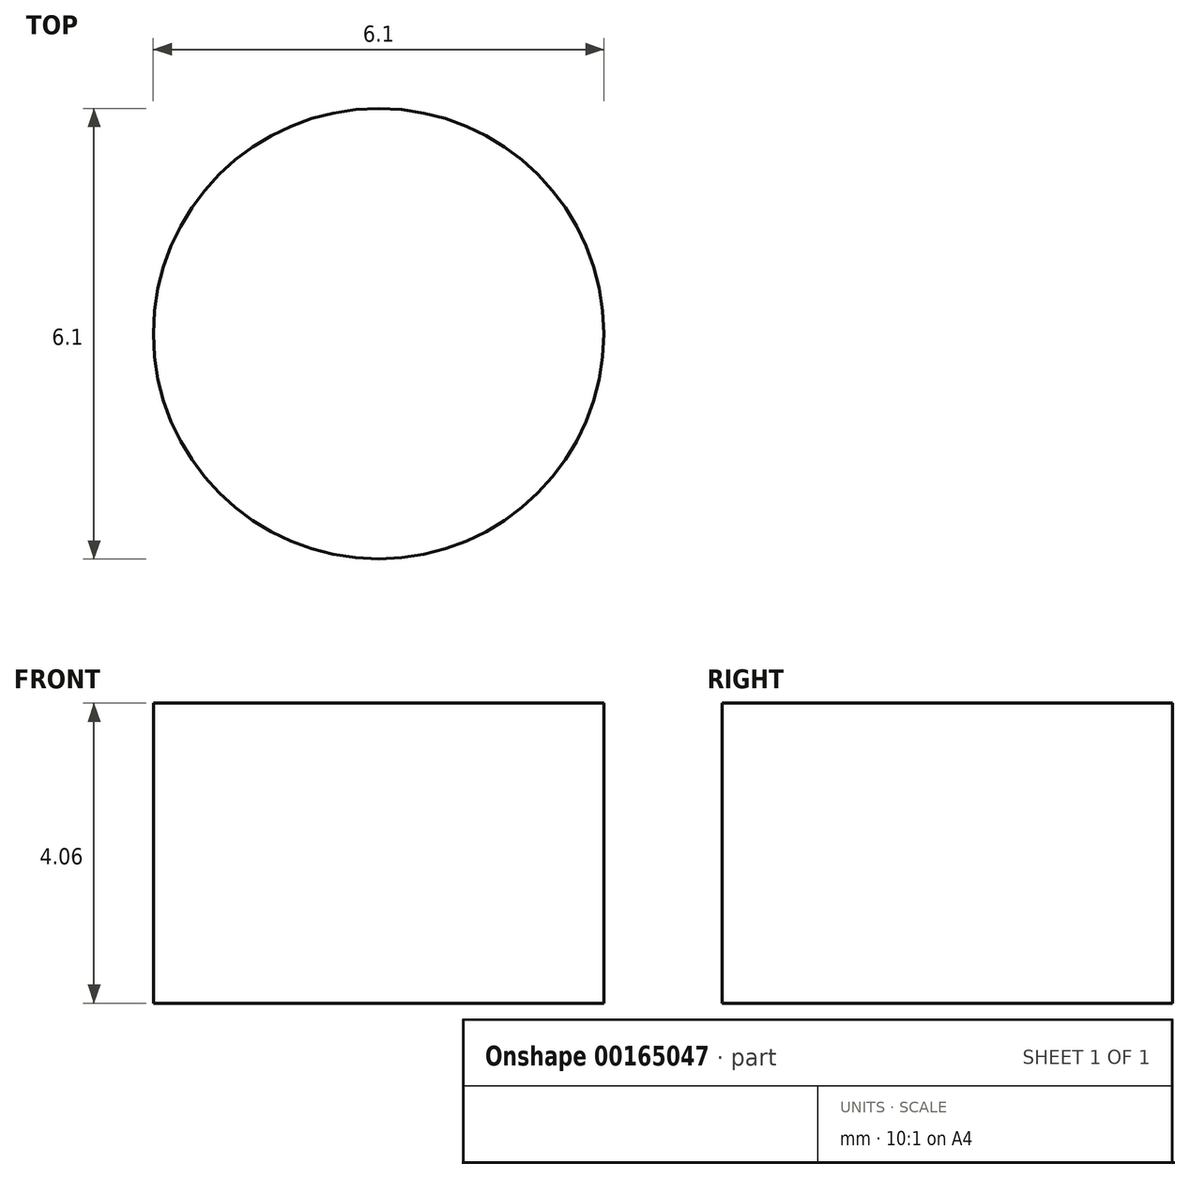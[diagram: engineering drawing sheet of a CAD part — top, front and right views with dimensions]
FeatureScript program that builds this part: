
annotation { "Feature Type Name" : "Feature", "Feature Type Description" : "" }
export const myFeature = defineFeature(function(context is Context, id is Id, definition is map)
    precondition{}
    {
        {
            var Q0;
            Q0=qCreatedBy(makeId("Top.planeOp"),FACE);
            var sketch = newSketch(context, id + "F0", { "sketchPlane" : qUnion([Q0])});
            skCircle(sketch, "E0", {"center": v(0, 0) * mm, "radius": 3.05 * mm});
            skSolve(sketch);
        }
        {
            var Q0;
            Q0 = qSketchRegion(id + "F0", true);
            extrude(context, id + "F1", {"entities" : qUnion([Q0]), "depth" : 4.06 * mm});
        }
    });
